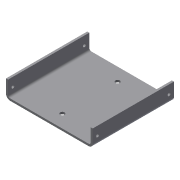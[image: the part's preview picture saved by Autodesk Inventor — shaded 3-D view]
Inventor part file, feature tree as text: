
AUTODESK INVENTOR PART (.ipt)
format: ipt  version: 2014 SP2 (Build 180246200, 246)  size: 127,488 bytes
history: native  units: in
note: dims shown in document units (in); Inventor stores cm internally (conversion verified against a paired STEP export)
features: sheet_metal_op x7, sketch x5, other x3, hole x2
ambient origin geometry x8: Origin, YZ Plane, XZ Plane, XY Plane, X Axis, Y Axis, Z Axis, Center Point
bodies: Solid1 (feature_tree)
feature tree (17):
  sheet_metal_op  "Face1"
  sheet_metal_op  "Flange1"
  sheet_metal_op  "Flange2"
  hole  "Hole1"  [1 undecoded]
  hole  "Hole2"  [1 undecoded]
  sketch  "Sketch1"  dims[d0=5.0in d1=4.685in]
  other  "Plate1"
  sketch  "Sketch2"  dims[d2=0.12in d3=0.12in]
  other  "Plate2"
  sheet_metal_op  "Bend1"
  sheet_metal_op  "Corner1"
  sketch  "Sketch3"  dims[d4=0.06in]
  other  "Plate3"
  sheet_metal_op  "Bend2"
  sheet_metal_op  "Corner2"
  sketch  "Sketch4"  dims[d5=0.24in]
  sketch  "Sketch5"  dims[d6=0.12in d7=1.0in d8=90.0deg d9=0.12in d10=0.48in d11=0.12in d12=0.12in d13=0.12in d14=0.06in d15=0.24in d16=0.12in d17=1.0in d18=90.0deg d19=0.12in d20=0.48in d21=0.12in d22=0.12in d23=0.75in d24=0.75in d25=0.25in d26=0.75in d27=0.375in d28=0.25in d29=0.5635in d30=0.12in d31=0.8108in d32=0.28in d33=0.28in d34=0.5in d35=0.5in d36=0.169in d37=0.75in d38=0.375in d39=0.25in d40=0.5635in d41=40.0in d42=0.8108in]
note: 2 required parameter values undecoded (feature->parameter linkage not recoverable at this tier; creation-order binding heuristic only, values carry confidence <= 0.55)
